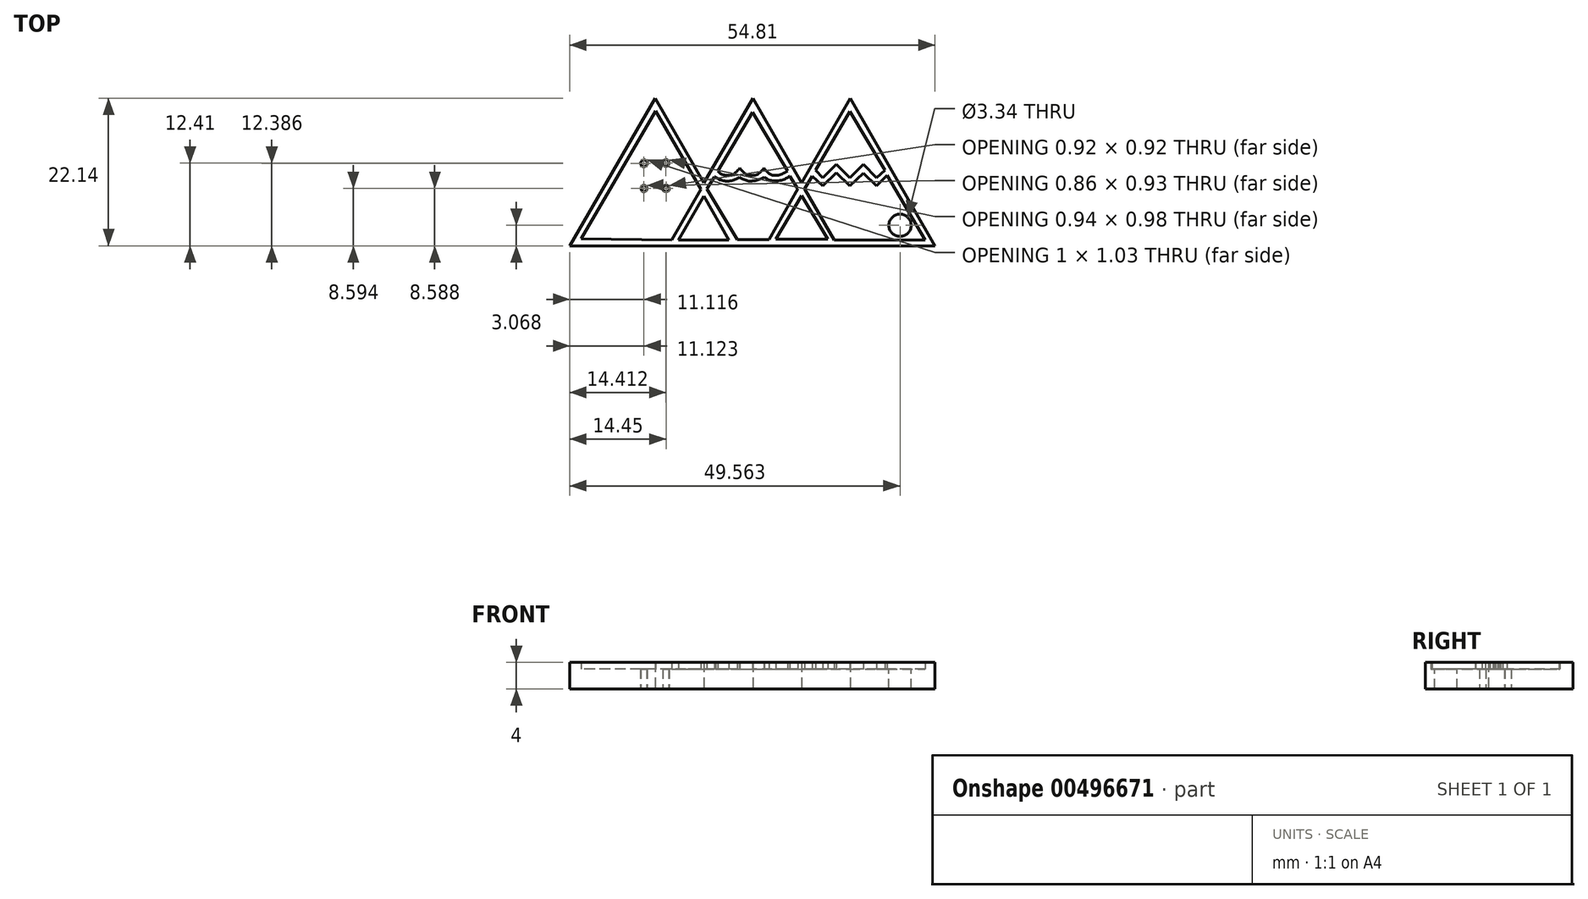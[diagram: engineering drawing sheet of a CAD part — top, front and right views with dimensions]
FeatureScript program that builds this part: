
annotation { "Feature Type Name" : "Feature", "Feature Type Description" : "" }
export const myFeature = defineFeature(function(context is Context, id is Id, definition is map)
    precondition{}
    {
        {
            var Q0;
            Q0=qCreatedBy(makeId("Top.planeOp"),FACE);
            var sketch = newSketch(context, id + "F0", { "sketchPlane" : qUnion([Q0])});
            skFitSpline(sketch, "E0", {"points": [v(-27.02, 0) * mm, v(-14.2, 22.14) * mm], "startDerivative": vector(12.81, 22.14) * mm, "endDerivative": vector(12.81, 22.14) * mm});
            skFitSpline(sketch, "E1", {"points": [v(-14.2, 22.14) * mm, v(-6.9, 9.44) * mm], "startDerivative": vector(7.31, -12.7) * mm, "endDerivative": vector(7.31, -12.7) * mm});
            skFitSpline(sketch, "E2", {"points": [v(-6.9, 9.44) * mm, v(0.49, 22.14) * mm], "startDerivative": vector(7.38, 12.7) * mm, "endDerivative": vector(7.38, 12.7) * mm});
            skFitSpline(sketch, "E3", {"points": [v(0.49, 22.14) * mm, v(7.77, 9.44) * mm], "startDerivative": vector(7.28, -12.7) * mm, "endDerivative": vector(7.28, -12.7) * mm});
            skFitSpline(sketch, "E4", {"points": [v(7.77, 9.44) * mm, v(15.06, 22.14) * mm], "startDerivative": vector(7.3, 12.7) * mm, "endDerivative": vector(7.3, 12.7) * mm});
            skFitSpline(sketch, "E5", {"points": [v(15.06, 22.14) * mm, v(27.79, 0) * mm], "startDerivative": vector(12.73, -22.14) * mm, "endDerivative": vector(12.73, -22.14) * mm});
            skFitSpline(sketch, "E6", {"points": [v(27.79, 0) * mm, v(-27.02, 0) * mm], "startDerivative": vector(-54.8, 0) * mm, "endDerivative": vector(-54.8, 0) * mm});
            skFitSpline(sketch, "E7", {"points": [v(-7.32, 8.5) * mm, v(-11.73, 0.89) * mm], "startDerivative": vector(-4.4, -7.62) * mm, "endDerivative": vector(-4.4, -7.62) * mm});
            skFitSpline(sketch, "E8", {"points": [v(-25.32, 1.03) * mm, v(-11.73, 0.89) * mm], "startDerivative": vector(13.6, -0.14) * mm, "endDerivative": vector(13.6, -0.14) * mm});
            skFitSpline(sketch, "E9", {"points": [v(-25.32, 1.03) * mm, v(-14.15, 20.2) * mm], "startDerivative": vector(11.17, 19.17) * mm, "endDerivative": vector(11.17, 19.17) * mm});
            skFitSpline(sketch, "E10", {"points": [v(-14.15, 20.2) * mm, v(-7.32, 8.5) * mm], "startDerivative": vector(6.83, -11.7) * mm, "endDerivative": vector(6.83, -11.7) * mm});
            skFitSpline(sketch, "E11", {"points": [v(-6.9, 7.5) * mm, v(-10.73, 0.89) * mm], "startDerivative": vector(-3.84, -6.6) * mm, "endDerivative": vector(-3.84, -6.6) * mm});
            skFitSpline(sketch, "E12", {"points": [v(-10.73, 0.89) * mm, v(-3.01, 0.89) * mm], "startDerivative": vector(7.72, 0) * mm, "endDerivative": vector(7.72, 0) * mm});
            skFitSpline(sketch, "E13", {"points": [v(-3.01, 0.7) * mm, v(-6.9, 7.5) * mm], "startDerivative": vector(-3.88, 6.8) * mm, "endDerivative": vector(-3.88, 6.8) * mm});
            skFitSpline(sketch, "E14", {"points": [v(-6.45, 8.53) * mm, v(-5.33, 10.3) * mm], "startDerivative": vector(1.13, 1.77) * mm, "endDerivative": vector(1.13, 1.77) * mm});
            skFitSpline(sketch, "E15", {"points": [v(-5.33, 10.3) * mm, v(-5.1, 10.3) * mm], "startDerivative": vector(0.22, 0) * mm, "endDerivative": vector(0.22, 0) * mm});
            skFitSpline(sketch, "E16", {"points": [v(-5.1, 10.3) * mm, v(-4.6, 9.96) * mm, v(-3.83, 9.74) * mm, v(-3.03, 9.72) * mm, v(-2.12, 9.98) * mm, v(-1.54, 10.3) * mm], "startDerivative": vector(2.66, -2.08) * mm, "endDerivative": vector(2.87, 1.8) * mm});
            skFitSpline(sketch, "E17", {"points": [v(-1.54, 10.3) * mm, v(-1.02, 9.98) * mm, v(-0.18, 9.72) * mm, v(0.4, 9.72) * mm, v(1.43, 9.94) * mm, v(2.16, 10.3) * mm], "startDerivative": vector(2.61, -1.9) * mm, "endDerivative": vector(3.27, 1.96) * mm});
            skFitSpline(sketch, "E18", {"points": [v(2.16, 10.3) * mm, v(2.64, 10.01) * mm, v(3.3, 9.78) * mm, v(3.93, 9.74) * mm, v(4.82, 9.86) * mm, v(5.55, 10.17) * mm, v(5.98, 10.45) * mm], "startDerivative": vector(2.96, -2.03) * mm, "endDerivative": vector(2.74, 1.93) * mm});
            skFitSpline(sketch, "E19", {"points": [v(5.98, 10.45) * mm, v(7.22, 8.54) * mm], "startDerivative": vector(1.24, -1.91) * mm, "endDerivative": vector(1.24, -1.91) * mm});
            skFitSpline(sketch, "E20", {"points": [v(7.22, 8.54) * mm, v(2.91, 0.92) * mm], "startDerivative": vector(-4.3, -7.63) * mm, "endDerivative": vector(-4.3, -7.63) * mm});
            skFitSpline(sketch, "E21", {"points": [v(2.91, 0.92) * mm, v(-1.9, 0.92) * mm], "startDerivative": vector(-4.8, 0) * mm, "endDerivative": vector(-4.8, 0) * mm});
            skFitSpline(sketch, "E22", {"points": [v(-6.45, 8.53) * mm, v(-1.9, 0.92) * mm], "startDerivative": vector(4.56, -7.62) * mm, "endDerivative": vector(4.56, -7.62) * mm});
            skFitSpline(sketch, "E23", {"points": [v(-15.95, 12.9) * mm, v(-16.15, 12.8) * mm, v(-16.37, 12.53) * mm, v(-16.32, 12.08) * mm, v(-16, 11.88) * mm, v(-15.58, 11.96) * mm, v(-15.4, 12.46) * mm, v(-15.62, 12.85) * mm, v(-15.95, 12.9) * mm]});
            skFitSpline(sketch, "E24", {"points": [v(-12.64, 12.9) * mm, v(-12.87, 12.84) * mm, v(-13.04, 12.63) * mm, v(-13.07, 12.33) * mm, v(-12.93, 12.03) * mm, v(-12.64, 11.92) * mm, v(-12.35, 11.98) * mm, v(-12.17, 12.22) * mm, v(-12.15, 12.54) * mm, v(-12.3, 12.84) * mm, v(-12.64, 12.9) * mm]});
            skFitSpline(sketch, "E25", {"points": [v(-15.94, 9.06) * mm, v(-16.1, 9.04) * mm, v(-16.26, 8.87) * mm, v(-16.33, 8.56) * mm, v(-16.17, 8.2) * mm, v(-15.94, 8.13) * mm, v(-15.68, 8.17) * mm, v(-15.51, 8.38) * mm, v(-15.48, 8.68) * mm, v(-15.6, 8.96) * mm, v(-15.94, 9.06) * mm]});
            skFitSpline(sketch, "E26", {"points": [v(-12.64, 9.05) * mm, v(-12.92, 8.98) * mm, v(-13.04, 8.61) * mm, v(-12.92, 8.24) * mm, v(-12.68, 8.13) * mm, v(-12.28, 8.2) * mm, v(-12.1, 8.58) * mm, v(-12.16, 8.84) * mm, v(-12.35, 9.01) * mm, v(-12.64, 9.05) * mm]});
            skFitSpline(sketch, "E27", {"points": [v(0.44, 20.06) * mm, v(-4.82, 11.23) * mm], "startDerivative": vector(-5.26, -8.83) * mm, "endDerivative": vector(-5.26, -8.83) * mm});
            skFitSpline(sketch, "E28", {"points": [v(-4.82, 11.23) * mm, v(-4.5, 10.93) * mm, v(-4.22, 10.75) * mm, v(-3.73, 10.6) * mm, v(-3.36, 10.58) * mm, v(-2.84, 10.6) * mm, v(-2.18, 10.95) * mm, v(-1.5, 11.65) * mm], "startDerivative": vector(2.6, -2.57) * mm, "endDerivative": vector(3.5, 3.86) * mm});
            skFitSpline(sketch, "E29", {"points": [v(-1.5, 11.65) * mm, v(-0.9, 10.99) * mm, v(-0.44, 10.68) * mm, v(0, 10.58) * mm, v(0.56, 10.58) * mm, v(1.2, 10.75) * mm, v(1.72, 11.15) * mm, v(2.15, 11.65) * mm], "startDerivative": vector(3.5, -4.23) * mm, "endDerivative": vector(2.86, 3.46) * mm});
            skFitSpline(sketch, "E30", {"points": [v(2.15, 11.65) * mm, v(2.46, 11.23) * mm, v(2.79, 10.93) * mm, v(3.1, 10.74) * mm, v(3.35, 10.62) * mm, v(3.68, 10.6) * mm, v(4.27, 10.58) * mm, v(4.82, 10.74) * mm, v(5.36, 11.06) * mm, v(5.65, 11.23) * mm], "startDerivative": vector(2.54, -3.56) * mm, "endDerivative": vector(2.82, 1.54) * mm});
            skFitSpline(sketch, "E31", {"points": [v(0.44, 20.06) * mm, v(5.65, 11.23) * mm], "startDerivative": vector(5.22, -8.83) * mm, "endDerivative": vector(5.22, -8.83) * mm});
            skFitSpline(sketch, "E32", {"points": [v(7.75, 7.55) * mm, v(3.92, 1) * mm], "startDerivative": vector(-3.83, -6.56) * mm, "endDerivative": vector(-3.83, -6.56) * mm});
            skFitSpline(sketch, "E33", {"points": [v(3.92, 1) * mm, v(11.7, 1) * mm], "startDerivative": vector(7.77, 0) * mm, "endDerivative": vector(7.77, 0) * mm});
            skFitSpline(sketch, "E34", {"points": [v(11.7, 1) * mm, v(7.75, 7.55) * mm], "startDerivative": vector(-3.94, 6.56) * mm, "endDerivative": vector(-3.94, 6.56) * mm});
            skFitSpline(sketch, "E35", {"points": [v(15.01, 20.18) * mm, v(9.84, 11.33) * mm], "startDerivative": vector(-5.18, -8.85) * mm, "endDerivative": vector(-5.18, -8.85) * mm});
            skFitSpline(sketch, "E36", {"points": [v(9.84, 11.33) * mm, v(10.98, 10.19) * mm], "startDerivative": vector(1.14, -1.15) * mm, "endDerivative": vector(1.14, -1.15) * mm});
            skFitSpline(sketch, "E37", {"points": [v(10.98, 10.19) * mm, v(12.99, 12.26) * mm], "startDerivative": vector(2.01, 2.07) * mm, "endDerivative": vector(2.01, 2.07) * mm});
            skFitSpline(sketch, "E38", {"points": [v(12.99, 12.26) * mm, v(15.02, 10.19) * mm], "startDerivative": vector(2.03, -2.07) * mm, "endDerivative": vector(2.03, -2.07) * mm});
            skFitSpline(sketch, "E39", {"points": [v(15.02, 10.19) * mm, v(17.03, 12.26) * mm], "startDerivative": vector(2.02, 2.07) * mm, "endDerivative": vector(2.02, 2.07) * mm});
            skFitSpline(sketch, "E40", {"points": [v(17.03, 12.26) * mm, v(19.03, 10.19) * mm], "startDerivative": vector(2, -2.07) * mm, "endDerivative": vector(2, -2.07) * mm});
            skFitSpline(sketch, "E41", {"points": [v(19.03, 10.19) * mm, v(20.25, 11.33) * mm], "startDerivative": vector(1.23, 1.15) * mm, "endDerivative": vector(1.23, 1.15) * mm});
            skFitSpline(sketch, "E42", {"points": [v(20.25, 11.33) * mm, v(15.01, 20.18) * mm], "startDerivative": vector(-5.24, 8.85) * mm, "endDerivative": vector(-5.24, 8.85) * mm});
            skFitSpline(sketch, "E43", {"points": [v(9.37, 10.44) * mm, v(8.2, 8.54) * mm], "startDerivative": vector(-1.16, -1.9) * mm, "endDerivative": vector(-1.16, -1.9) * mm});
            skFitSpline(sketch, "E44", {"points": [v(8.2, 8.54) * mm, v(12.68, 0.86) * mm], "startDerivative": vector(4.48, -7.68) * mm, "endDerivative": vector(4.48, -7.68) * mm});
            skFitSpline(sketch, "E45", {"points": [v(12.68, 0.86) * mm, v(26.29, 0.86) * mm], "startDerivative": vector(13.6, 0) * mm, "endDerivative": vector(13.6, 0) * mm});
            skFitSpline(sketch, "E46", {"points": [v(26.29, 0.86) * mm, v(20.61, 10.57) * mm], "startDerivative": vector(-5.67, 9.71) * mm, "endDerivative": vector(-5.67, 9.71) * mm});
            skFitSpline(sketch, "E47", {"points": [v(20.61, 10.57) * mm, v(19.03, 9) * mm], "startDerivative": vector(-1.59, -1.57) * mm, "endDerivative": vector(-1.59, -1.57) * mm});
            skFitSpline(sketch, "E48", {"points": [v(19.03, 9) * mm, v(17.03, 10.89) * mm], "startDerivative": vector(-2, 1.9) * mm, "endDerivative": vector(-2, 1.9) * mm});
            skFitSpline(sketch, "E49", {"points": [v(17.03, 10.89) * mm, v(15.02, 9) * mm], "startDerivative": vector(-2.02, -1.9) * mm, "endDerivative": vector(-2.02, -1.9) * mm});
            skFitSpline(sketch, "E50", {"points": [v(15.02, 9) * mm, v(12.99, 10.98) * mm], "startDerivative": vector(-2.03, 1.98) * mm, "endDerivative": vector(-2.03, 1.98) * mm});
            skFitSpline(sketch, "E51", {"points": [v(12.99, 10.98) * mm, v(10.98, 9) * mm], "startDerivative": vector(-2.01, -1.98) * mm, "endDerivative": vector(-2.01, -1.98) * mm});
            skFitSpline(sketch, "E52", {"points": [v(10.98, 9) * mm, v(9.37, 10.44) * mm], "startDerivative": vector(-1.6, 1.44) * mm, "endDerivative": vector(-1.6, 1.44) * mm});
            skSolve(sketch);
        }
        {
            var Q0;
            Q0 = qSketchRegion(id + "F0", true);
            var Q1;
            Q1=makeQuery(id+"F0.imprint","IMPRINT",FACE,{"disambiguationData":[TD([[makeQuery(id+"F0.imprint","IMPRINT",EDGE,{"derivedFrom":sQuery(id+"F0.wireOp",EDGE,"E7")}),-1.0]])]});
            var Q2;
            {var subQ0=sQuery(id+"F0.wireOp",EDGE,"E11");Q2=makeQuery(id+"F0.imprint","IMPRINT",FACE,{"disambiguationData":[TD([[makeQuery(id+"F0.imprint","IMPRINT",EDGE,{"derivedFrom":subQ0}),1.0]])]});}
            var Q3;
            Q3=makeQuery(id+"F0.imprint","IMPRINT",FACE,{"disambiguationData":[TD([[makeQuery(id+"F0.imprint","IMPRINT",EDGE,{"derivedFrom":sQuery(id+"F0.wireOp",EDGE,"E14")}),-1.0]])]});
            var Q4;
            Q4=makeQuery(id+"F0.imprint","IMPRINT",FACE,{"disambiguationData":[TD([[makeQuery(id+"F0.imprint","IMPRINT",EDGE,{"derivedFrom":sQuery(id+"F0.wireOp",EDGE,"E27")}),1.0]])]});
            var Q5;
            Q5=makeQuery(id+"F0.imprint","IMPRINT",FACE,{"disambiguationData":[TD([[makeQuery(id+"F0.imprint","IMPRINT",EDGE,{"derivedFrom":sQuery(id+"F0.wireOp",EDGE,"E35")}),1.0]])]});
            var Q6;
            Q6=makeQuery(id+"F0.imprint","IMPRINT",FACE,{"disambiguationData":[TD([[makeQuery(id+"F0.imprint","IMPRINT",EDGE,{"derivedFrom":sQuery(id+"F0.wireOp",EDGE,"E43")}),1.0]])]});
            var Q7;
            Q7=makeQuery(id+"F0.imprint","IMPRINT",FACE,{"disambiguationData":[TD([[makeQuery(id+"F0.imprint","IMPRINT",EDGE,{"derivedFrom":sQuery(id+"F0.wireOp",EDGE,"E32")}),1.0]])]});
            extrude(context, id + "F1", {"entities" : qUnion([Q0, Q1, Q2, Q3, Q4, Q5, Q6, Q7]), "depth" : 3 * mm, "offsetDistance" : 25 * mm});
        }
        {
            var Q0;
            Q0 = qSketchRegion(id + "F0", true);
            extrude(context, id + "F2", {"entities" : qUnion([Q0]), "operationType" : NewBodyOperationType.ADD, "depth" : 4 * mm, "offsetDistance" : 25 * mm});
        }
        {
            var Q0;
            Q0=makeQuery(id+"F2.boolean.opBoolean","SPLIT",FACE,{"disambiguationData":[TD([makeQuery(id+"F2.opExtrude","SWEPT_FACE",FACE,{"disambiguationData":[OSD([sQuery(id+"F0.wireOp",EDGE,"E43")])]})])],"derivedFrom":makeQuery(id+"F1.opExtrude","CAP_FACE",FACE,{"disambiguationData":[OSD([sQuery(id+"F0.wireOp",EDGE,"E0"),sQuery(id+"F0.wireOp",EDGE,"E1"),sQuery(id+"F0.wireOp",EDGE,"E2"),sQuery(id+"F0.wireOp",EDGE,"E3"),sQuery(id+"F0.wireOp",EDGE,"E4"),sQuery(id+"F0.wireOp",EDGE,"E5"),sQuery(id+"F0.wireOp",EDGE,"E6"),sQuery(id+"F0.wireOp",EDGE,"E23"),sQuery(id+"F0.wireOp",EDGE,"E24"),sQuery(id+"F0.wireOp",EDGE,"E25"),sQuery(id+"F0.wireOp",EDGE,"E26")])],"isStart":false})});
            var sketch = newSketch(context, id + "F3", { "sketchPlane" : qUnion([Q0])});
            skCircle(sketch, "E53", {"center": v(22.54, 3.07) * mm, "radius": 1.67 * mm});
            skSolve(sketch);
        }
        {
            var Q0;
            Q0 = qSketchRegion(id + "F3", true);
            extrude(context, id + "F4", {"entities" : qUnion([Q0]), "operationType" : NewBodyOperationType.REMOVE, "oppositeDirection" : true, "depth" : 25 * mm, "offsetDistance" : 25 * mm});
        }
    });
